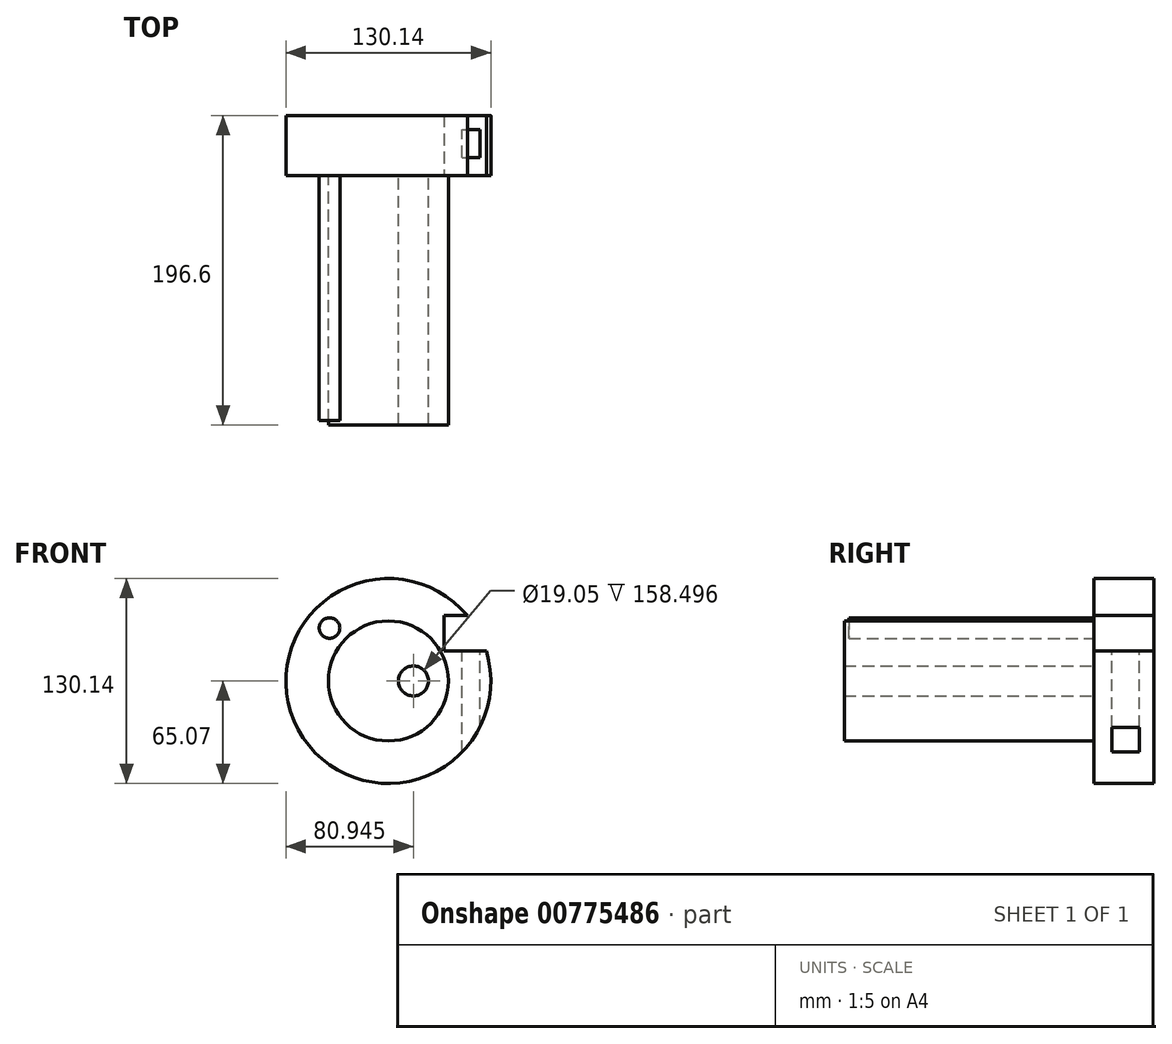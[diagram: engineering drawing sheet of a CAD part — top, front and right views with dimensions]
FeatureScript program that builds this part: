
annotation { "Feature Type Name" : "Feature", "Feature Type Description" : "" }
export const myFeature = defineFeature(function(context is Context, id is Id, definition is map)
    precondition{}
    {
        {
            var Q0;
            Q0=qCreatedBy(makeId("Front.planeOp"),FACE);
            var sketch = newSketch(context, id + "F0", { "sketchPlane" : qUnion([Q0])});
            skCircle(sketch, "E0", {"center": v(0, 0) * mm, "radius": 65.07 * mm});
            skSolve(sketch);
        }
        {
            var Q0;
            Q0 = qSketchRegion(id + "F0", true);
            extrude(context, id + "F1", {"entities" : qUnion([Q0]), "depth" : 38.1 * mm, "offsetDistance" : 25.4 * mm});
        }
        {
            var Q0;
            Q0=makeQuery(id+"F1.opExtrude","CAP_FACE",FACE,{"disambiguationData":[OSD([sQuery(id+"F0.wireOp",EDGE,"E0")])],"isStart":false});
            var sketch = newSketch(context, id + "F2", { "sketchPlane" : qUnion([Q0])});
            skCircle(sketch, "E1", {"center": v(0, 0) * mm, "radius": 38.1 * mm});
            skCircle(sketch, "E2", {"center": v(15.88, 0) * mm, "radius": 9.53 * mm});
            skSolve(sketch);
        }
        {
            var Q0;
            Q0 = qSketchRegion(id + "F2", true);
            extrude(context, id + "F3", {"entities" : qUnion([Q0]), "operationType" : NewBodyOperationType.ADD, "depth" : 158.5 * mm, "offsetDistance" : 25.4 * mm});
        }
        {
            var Q0;
            {var subQ0=sQuery(id+"F0.wireOp",EDGE,"E0");Q0=makeQuery(id+"F3.boolean.opBoolean","SPLIT",FACE,{"disambiguationData":[TD([makeQuery(id+"F1.opExtrude","SWEPT_FACE",FACE,{"disambiguationData":[OSD([subQ0])]})])],"derivedFrom":makeQuery(id+"F1.opExtrude","CAP_FACE",FACE,{"disambiguationData":[OSD([subQ0])],"isStart":false})});}
            var sketch = newSketch(context, id + "F4", { "sketchPlane" : qUnion([Q0])});
            skCircle(sketch, "E3", {"center": v(-37.39, 33.61) * mm, "radius": 6.54 * mm});
            skSolve(sketch);
        }
        {
            var Q0;
            Q0 = qSketchRegion(id + "F4", true);
            extrude(context, id + "F5", {"entities" : qUnion([Q0]), "operationType" : NewBodyOperationType.ADD, "depth" : 155.7 * mm, "offsetDistance" : 25.4 * mm});
        }
        {
            var Q0;
            {var subQ0=sQuery(id+"F0.wireOp",EDGE,"E0");Q0=makeQuery(id+"F3.boolean.opBoolean","SPLIT",FACE,{"disambiguationData":[TD([makeQuery(id+"F1.opExtrude","SWEPT_FACE",FACE,{"disambiguationData":[OSD([subQ0])]})])],"derivedFrom":makeQuery(id+"F1.opExtrude","CAP_FACE",FACE,{"disambiguationData":[OSD([subQ0])],"isStart":false})});}
            var sketch = newSketch(context, id + "F6", { "sketchPlane" : qUnion([Q0])});
            skLineSegment(sketch, "E4.bottom", {"start": v(35.43, 41.47) * mm, "end": v(135.61, 41.47) * mm});
            skLineSegment(sketch, "E4.top", {"start": v(35.43, 19.06) * mm, "end": v(135.61, 19.06) * mm});
            skLineSegment(sketch, "E4.left", {"start": v(35.43, 41.47) * mm, "end": v(35.43, 19.06) * mm});
            skLineSegment(sketch, "E4.right", {"start": v(135.61, 41.47) * mm, "end": v(135.61, 19.06) * mm});
            skSolve(sketch);
        }
        {
            var Q0;
            Q0 = qSketchRegion(id + "F6", true);
            extrude(context, id + "F7", {"entities" : qUnion([Q0]), "operationType" : NewBodyOperationType.REMOVE, "endBound" : BoundingType.THROUGH_ALL, "oppositeDirection" : true, "depth" : 25.4 * mm, "offsetDistance" : 25.4 * mm});
        }
        {
            var Q0;
            Q0=makeQuery(id+"F7.boolean.opBoolean","COPY",FACE,{"derivedFrom":makeQuery(id+"F7.opExtrude","SWEPT_FACE",FACE,{"disambiguationData":[OSD([sQuery(id+"F6.wireOp",EDGE,"E4.top")])]})});
            var sketch = newSketch(context, id + "F8", { "sketchPlane" : qUnion([Q0])});
            skLineSegment(sketch, "E5.bottom", {"start": v(46.83, -26.62) * mm, "end": v(58.04, -26.62) * mm});
            skLineSegment(sketch, "E5.top", {"start": v(46.83, -9.08) * mm, "end": v(58.04, -9.08) * mm});
            skLineSegment(sketch, "E5.left", {"start": v(46.83, -26.62) * mm, "end": v(46.83, -9.08) * mm});
            skLineSegment(sketch, "E5.right", {"start": v(58.04, -26.62) * mm, "end": v(58.04, -9.08) * mm});
            skSolve(sketch);
        }
        {
            var Q0;
            Q0 = qSketchRegion(id + "F8", true);
            extrude(context, id + "F9", {"entities" : qUnion([Q0]), "operationType" : NewBodyOperationType.REMOVE, "endBound" : BoundingType.THROUGH_ALL, "oppositeDirection" : true, "depth" : 25.4 * mm, "offsetDistance" : 25.4 * mm});
        }
    });
